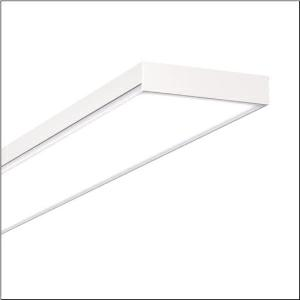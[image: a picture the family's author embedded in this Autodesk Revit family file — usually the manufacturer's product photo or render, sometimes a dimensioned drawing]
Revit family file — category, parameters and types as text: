
# Revit family: apollon_31_surface_51mp25wd2441wa
name_source: partatom
category: Lighting Fixtures
units: mm (PartAtom-declared; Revit-internal decimal feet)

## family parameters
Cut with Voids When Loaded = No
Host = Face
Light Source = No
Part Type = Normal
Room Calculation Point = No
Round Connector Dimension = Use Diameter
Shared = No

## types (1)
- Apollon 31 Surface (1 x LED, 3800 lm, 28 W, 4000K)
    Apparent Load = 28 VA
    CIE Flux Codes = 61 87 97 97 100
    Color Rendering = 80
    Color Temperature = 4000K
    Default Elevation = 1800 mm
    Description = Apollon 31 Surface, office luminaire, primary optical cover: micro prismatic cover, of PMMA, light emission: direct distribution, primary light characteristic: symmetric, installation type: surface-mounted, LED, rated luminous flux: 3.800lm, luminous efficacy: 134lm/W, light colour: 840, colour temperature: 4000K, control gear: DALI 2, with terminal, 5-pole, mains connection: 220..240V, AC, 50/60Hz, rated input power: 28W, housing, of sheet steel, coated, traffic white (RAL 9016), length: 1.245mm, width: 200mm, height: 44mm, protection rating (complete): IP20, protection rating (on room side): IP40, protection rating (lamp compartment, on room side): IP40, insulation class (complete): insulation class I (protective earthing), certification: CE, ENEC, UKCA, impact resistance: IK02, permissible operating ambient temperature: -20..+40°C, standard: EN 60598-2-22, packaging unit: 1 piece
    Height = 44 mm
    Lamp = 1 x LED
    Lamp Light Flux = 3800 lm
    Lamp Power = 28 W
    Lamp count = 1
    Length = 1245 mm
    Luminous efficacy = 136 lm/W
    Manufacturer = Siteco
    ModVariant = No
    Model = 51MP25WD2441WA
    Mounting Place = Ceiling
    Mounting Type = Surface mounted
    Number of Poles = 1
    OnlyDefault = Yes
    Power Factor = 1
    Product Name = Apollon 31 Surface
    Product group = office luminaire | ceiling mounted
    ProductGroupID = 301
    Protection Class = Protection class I
    Protection Degree = IP 20
    RLX_Detail_Level = 1
    RLX_Emergency_Light_Flux = 0 lm
    RLX_Emergency_Type = 0
    RLX_Emergency_Type_DB = No
    RlxData = <blob elided: 20805 chars, md5=97b5268f>
    Socket = socket
    Standby Power = 0 W
    System Light Flux = 3800 lm
    System Power = 28 W
    Type Comments = Product without accessories
    Type Image = l_1313658.jpg
    URL = http://relux.com
    VarID = ---
    Voltage = 0 V
    Weight = 0.00 kg
    Width = 200 mm  [stored 0.656168 ft]

note: [stored X ft] marks values corroborated as IEEE doubles in the binary element streams (Revit-internal decimal feet)

## geometry (parser evidence)
native form markers: Blend x4, Sweep x11
no freeform markers — native parametric forms only
